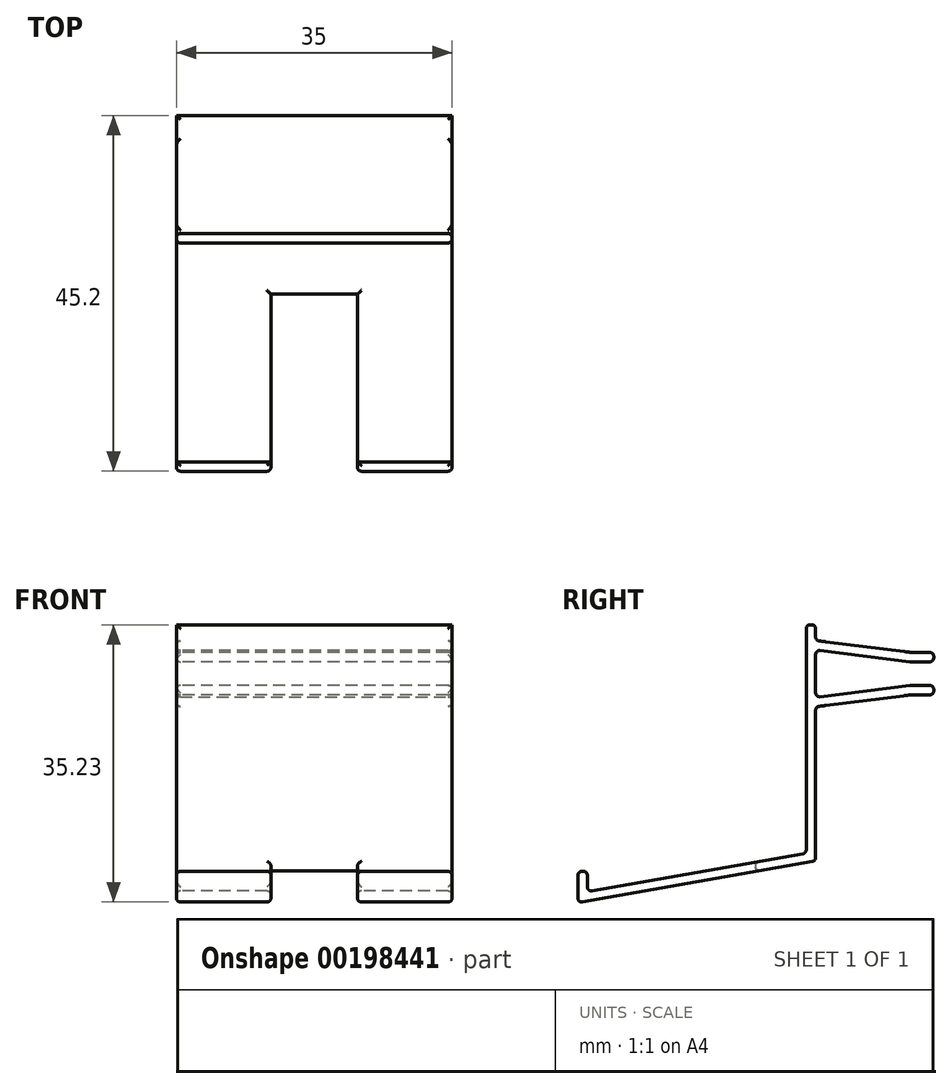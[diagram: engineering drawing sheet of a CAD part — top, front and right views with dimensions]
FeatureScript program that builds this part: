
annotation { "Feature Type Name" : "Feature", "Feature Type Description" : "" }
export const myFeature = defineFeature(function(context is Context, id is Id, definition is map)
    precondition{}
    {
        {
            var Q0;
            Q0=qCreatedBy(makeId("Right.planeOp"),FACE);
            var sketch = newSketch(context, id + "F0", { "sketchPlane" : qUnion([Q0])});
            skLineSegment(sketch, "E0", {"start": v(-23.91, -0.15) * mm, "end": v(23.71, -0.15) * mm, "construction": true});
            skLineSegment(sketch, "E1", {"start": v(-8.31, 4.06) * mm, "end": v(3.76, 2.55) * mm});
            skLineSegment(sketch, "E2", {"start": v(3.69, 1.35) * mm, "end": v(-8.31, 2.85) * mm});
            skLineSegment(sketch, "E3", {"start": v(-8.31, 4.06) * mm, "end": v(-8.31, -0.15) * mm, "construction": true});
            skLineSegment(sketch, "E4.bottom", {"start": v(3.69, 1.35) * mm, "end": v(6.69, 1.35) * mm});
            skLineSegment(sketch, "E4.top", {"start": v(3.76, 2.55) * mm, "end": v(6.69, 2.55) * mm});
            skLineSegment(sketch, "E4.right", {"start": v(6.69, 1.35) * mm, "end": v(6.69, 2.55) * mm});
            skLineSegment(sketch, "E5.MirrorCS", {"start": v(3.69, -1.65) * mm, "end": v(6.69, -1.65) * mm});
            skLineSegment(sketch, "E6.MirrorCS", {"start": v(3.69, -1.65) * mm, "end": v(-8.31, -3.15) * mm});
            skLineSegment(sketch, "E7.MirrorCS", {"start": v(-8.31, -4.36) * mm, "end": v(3.76, -2.85) * mm});
            skLineSegment(sketch, "E8.MirrorCS", {"start": v(6.69, -1.65) * mm, "end": v(6.69, -2.85) * mm});
            skLineSegment(sketch, "E9.MirrorCS", {"start": v(3.76, -2.85) * mm, "end": v(6.69, -2.85) * mm});
            skLineSegment(sketch, "E10", {"start": v(-8.31, 4.06) * mm, "end": v(-8.31, 6.06) * mm});
            skLineSegment(sketch, "E11", {"start": v(-8.31, 6.06) * mm, "end": v(-9.51, 6.06) * mm});
            skLineSegment(sketch, "E12", {"start": v(-9.51, 6.06) * mm, "end": v(-9.51, -22.95) * mm});
            skLineSegment(sketch, "E13", {"start": v(-9.51, -22.95) * mm, "end": v(-37.31, -27.85) * mm});
            skLineSegment(sketch, "E14", {"start": v(-38.51, -28.07) * mm, "end": v(-38.51, -29.27) * mm});
            skLineSegment(sketch, "E15", {"start": v(-38.51, -29.27) * mm, "end": v(-8.31, -23.94) * mm});
            skLineSegment(sketch, "E16", {"start": v(-38.51, -29.27) * mm, "end": v(-38.51, -25.27) * mm});
            skLineSegment(sketch, "E17", {"start": v(-38.51, -25.27) * mm, "end": v(-37.31, -25.27) * mm});
            skLineSegment(sketch, "E18", {"start": v(-37.31, -25.27) * mm, "end": v(-37.31, -27.85) * mm});
            skLineSegment(sketch, "E19", {"start": v(-8.31, -23.94) * mm, "end": v(-8.31, -4.36) * mm});
            skLineSegment(sketch, "E20", {"start": v(-8.31, -3.15) * mm, "end": v(-8.31, 2.85) * mm});
            skSolve(sketch);
        }
        {
            var Q0;
            Q0=makeQuery(id+"F0.imprint","IMPRINT",FACE,{"disambiguationData":[TD([[makeQuery(id+"F0.imprint","IMPRINT",EDGE,{"derivedFrom":sQuery(id+"F0.wireOp",EDGE,"E1")}),-1.0]])]});
            extrude(context, id + "F1", {"entities" : qUnion([Q0]), "endBound" : BoundingType.SYMMETRIC, "depth" : 35 * mm});
        }
        {
            var Q0;
            Q0=makeQuery(id+"F1.opExtrude","SWEPT_FACE",FACE,{"disambiguationData":[OSD([sQuery(id+"F0.wireOp",EDGE,"E13")])]});
            var sketch = newSketch(context, id + "F2", { "sketchPlane" : qUnion([Q0])});
            skLineSegment(sketch, "E21.bottom", {"start": v(5.5, -20) * mm, "end": v(-5.5, -20) * mm});
            skLineSegment(sketch, "E21.top", {"start": v(5.5, -45) * mm, "end": v(-5.5, -45) * mm});
            skLineSegment(sketch, "E21.left", {"start": v(5.5, -20) * mm, "end": v(5.5, -45) * mm});
            skLineSegment(sketch, "E21.right", {"start": v(-5.5, -20) * mm, "end": v(-5.5, -45) * mm});
            skPoint(sketch, "E21.middle", {"position": v(0, -32.5) * mm});
            skSolve(sketch);
        }
        {
            var Q0;
            {var subQ0=sQuery(id+"F2.wireOp",EDGE,"E21.top");Q0=makeQuery(id+"F2.imprint","IMPRINT",FACE,{"disambiguationData":[TD([[makeQuery(id+"F2.imprint","IMPRINT",EDGE,{"derivedFrom":subQ0}),-1.0]])]});}
            var Q1;
            {var subQ0=sQuery(id+"F2.wireOp",EDGE,"E21.bottom");Q1=makeQuery(id+"F2.imprint","IMPRINT",FACE,{"disambiguationData":[TD([[makeQuery(id+"F2.imprint","IMPRINT",EDGE,{"derivedFrom":subQ0}),1.0]])]});}
            extrude(context, id + "F3", {"entities" : qUnion([Q0, Q1]), "operationType" : NewBodyOperationType.REMOVE, "endBound" : BoundingType.SYMMETRIC, "depth" : 25 * mm});
        }
        {
            var Q0;
            Q0=makeQuery(id+"F1.opExtrude","SWEPT_FACE",FACE,{"disambiguationData":[OSD([sQuery(id+"F0.wireOp",EDGE,"E12")])]});
            var Q1;
            Q1=makeQuery(id+"F1.opExtrude","SWEPT_FACE",FACE,{"disambiguationData":[OSD([sQuery(id+"F0.wireOp",EDGE,"E13")])]});
            var Q2;
            Q2=makeQuery(id+"F1.opExtrude","SWEPT_FACE",FACE,{"disambiguationData":[OSD([sQuery(id+"F0.wireOp",EDGE,"E16")])]});
            var Q3;
            Q3=makeQuery(id+"F1.opExtrude","SWEPT_FACE",FACE,{"disambiguationData":[OSD([sQuery(id+"F0.wireOp",EDGE,"E17")])]});
            var Q4;
            Q4=makeQuery(id+"F1.opExtrude","SWEPT_FACE",FACE,{"disambiguationData":[OSD([sQuery(id+"F0.wireOp",EDGE,"E15")])]});
            var Q5;
            Q5=makeQuery(id+"F1.opExtrude","SWEPT_FACE",FACE,{"disambiguationData":[OSD([sQuery(id+"F0.wireOp",EDGE,"E19")])]});
            var Q6;
            Q6=makeQuery(id+"F1.opExtrude","SWEPT_FACE",FACE,{"disambiguationData":[OSD([sQuery(id+"F0.wireOp",EDGE,"E10")])]});
            var Q7;
            Q7=makeQuery(id+"F1.opExtrude","SWEPT_FACE",FACE,{"disambiguationData":[OSD([sQuery(id+"F0.wireOp",EDGE,"E4.top")])]});
            var Q8;
            Q8=makeQuery(id+"F1.opExtrude","SWEPT_FACE",FACE,{"disambiguationData":[OSD([sQuery(id+"F0.wireOp",EDGE,"E4.bottom")])]});
            var Q9;
            Q9=makeQuery(id+"F1.opExtrude","SWEPT_FACE",FACE,{"disambiguationData":[OSD([sQuery(id+"F0.wireOp",EDGE,"E9.MirrorCS")])]});
            var Q10;
            Q10=makeQuery(id+"F1.opExtrude","SWEPT_FACE",FACE,{"disambiguationData":[OSD([sQuery(id+"F0.wireOp",EDGE,"E5.MirrorCS")])]});
            var Q11;
            Q11=makeQuery(id+"F1.opExtrude","SWEPT_FACE",FACE,{"disambiguationData":[OSD([sQuery(id+"F0.wireOp",EDGE,"E2")])]});
            var Q12;
            Q12=makeQuery(id+"F1.opExtrude","SWEPT_FACE",FACE,{"disambiguationData":[OSD([sQuery(id+"F0.wireOp",EDGE,"E6.MirrorCS")])]});
            fillet(context, id + "F4", {"entities" : qUnion([Q0, Q1, Q2, Q3, Q4, Q5, Q6, Q7, Q8, Q9, Q10, Q11, Q12]), "radius" : 0.5 * mm, "tangentPropagation" : true, "allowEdgeOverflow" : false});
        }
    });
